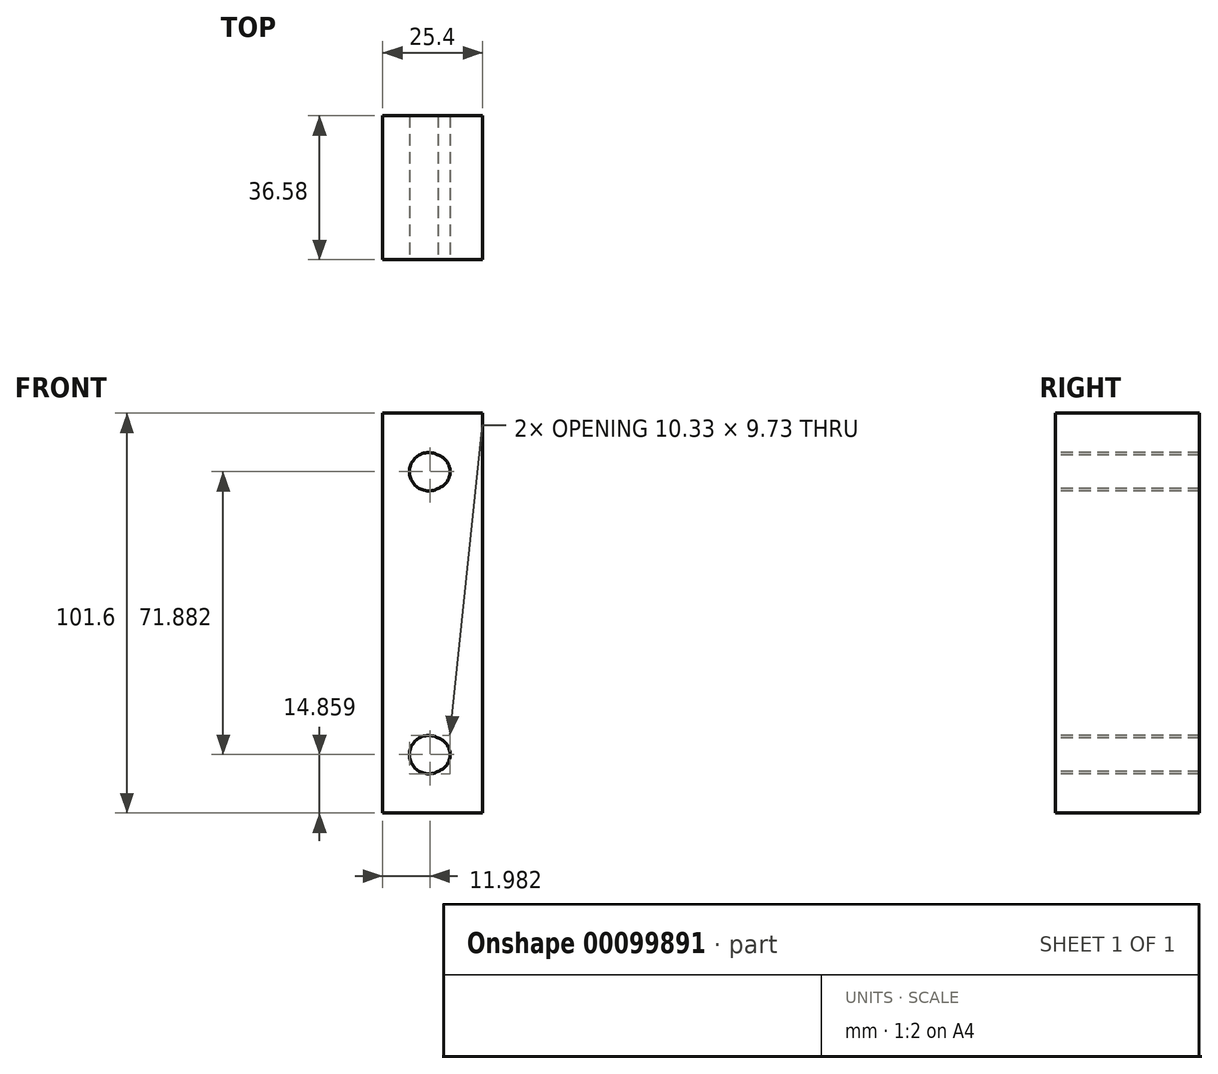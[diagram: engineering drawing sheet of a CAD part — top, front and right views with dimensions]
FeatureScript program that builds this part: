
annotation { "Feature Type Name" : "Feature", "Feature Type Description" : "" }
export const myFeature = defineFeature(function(context is Context, id is Id, definition is map)
    precondition{}
    {
        {
            var Q0;
            Q0=qCreatedBy(makeId("Front.planeOp"),FACE);
            var sketch = newSketch(context, id + "F0", { "sketchPlane" : qUnion([Q0])});
            skLineSegment(sketch, "E0.bottom", {"start": v(12.7, 50.8) * mm, "end": v(-12.7, 50.8) * mm});
            skLineSegment(sketch, "E0.top", {"start": v(12.7, -50.8) * mm, "end": v(-12.7, -50.8) * mm});
            skLineSegment(sketch, "E0.left", {"start": v(12.7, 50.8) * mm, "end": v(12.7, -50.8) * mm});
            skLineSegment(sketch, "E0.right", {"start": v(-12.7, 50.8) * mm, "end": v(-12.7, -50.8) * mm});
            skPoint(sketch, "E0.middle", {"position": v(0, 0) * mm});
            skPoint(sketch, "E1", {"position": v(0, 35.94) * mm});
            skPoint(sketch, "E2", {"position": v(0, -35.94) * mm});
            skPoint(sketch, "E3", {"position": v(-1.02, 35.94) * mm});
            skPoint(sketch, "E4", {"position": v(-1.02, -35.94) * mm});
            skSolve(sketch);
        }
        {
            var Q0;
            Q0 = qSketchRegion(id + "F0", true);
            extrude(context, id + "F1", {"entities" : qUnion([Q0]), "oppositeDirection" : true, "depth" : 36.58 * mm});
        }
        {
            var Q0;
            Q0=sQuery(id+"F0.wireOp",VERTEX,"E1");
            var Q1;
            Q1=sQuery(id+"F0.wireOp",VERTEX,"E2");
            var Q2;
            Q2=makeQuery(id+"F1.opExtrude","SWEPT_BODY",BODY,{"disambiguationData":[OSD([sQuery(id+"F0.wireOp",EDGE,"E0.bottom"),sQuery(id+"F0.wireOp",EDGE,"E0.top"),sQuery(id+"F0.wireOp",EDGE,"E0.left"),sQuery(id+"F0.wireOp",EDGE,"E0.right")])]});
            hole(context, id + "F2", {"style" : HoleStyle.SIMPLE, "endStyle" : HoleEndStyle.THROUGH, "holeDiameter" : 8.9 * mm, "isTappedThrough" : true, "tappedDepth" : 12.7 * mm, "tapClearance" : 3, "startFromSketch" : true, "locations" : qUnion([Q0, Q1]), "scope" : qUnion([Q2])});
        }
        {
            var Q0;
            Q0=sQuery(id+"F0.wireOp",VERTEX,"E3");
            var Q1;
            Q1=sQuery(id+"F0.wireOp",VERTEX,"E4");
            var Q2;
            Q2=makeQuery(id+"F1.opExtrude","SWEPT_BODY",BODY,{"disambiguationData":[OSD([sQuery(id+"F0.wireOp",EDGE,"E0.bottom"),sQuery(id+"F0.wireOp",EDGE,"E0.top"),sQuery(id+"F0.wireOp",EDGE,"E0.left"),sQuery(id+"F0.wireOp",EDGE,"E0.right")])]});
            hole(context, id + "F3", {"style" : HoleStyle.SIMPLE, "endStyle" : HoleEndStyle.THROUGH, "holeDiameter" : 9.73 * mm, "isTappedThrough" : true, "tappedDepth" : 12.7 * mm, "tapClearance" : 3, "startFromSketch" : true, "locations" : qUnion([Q0, Q1]), "scope" : qUnion([Q2])});
        }
    });
